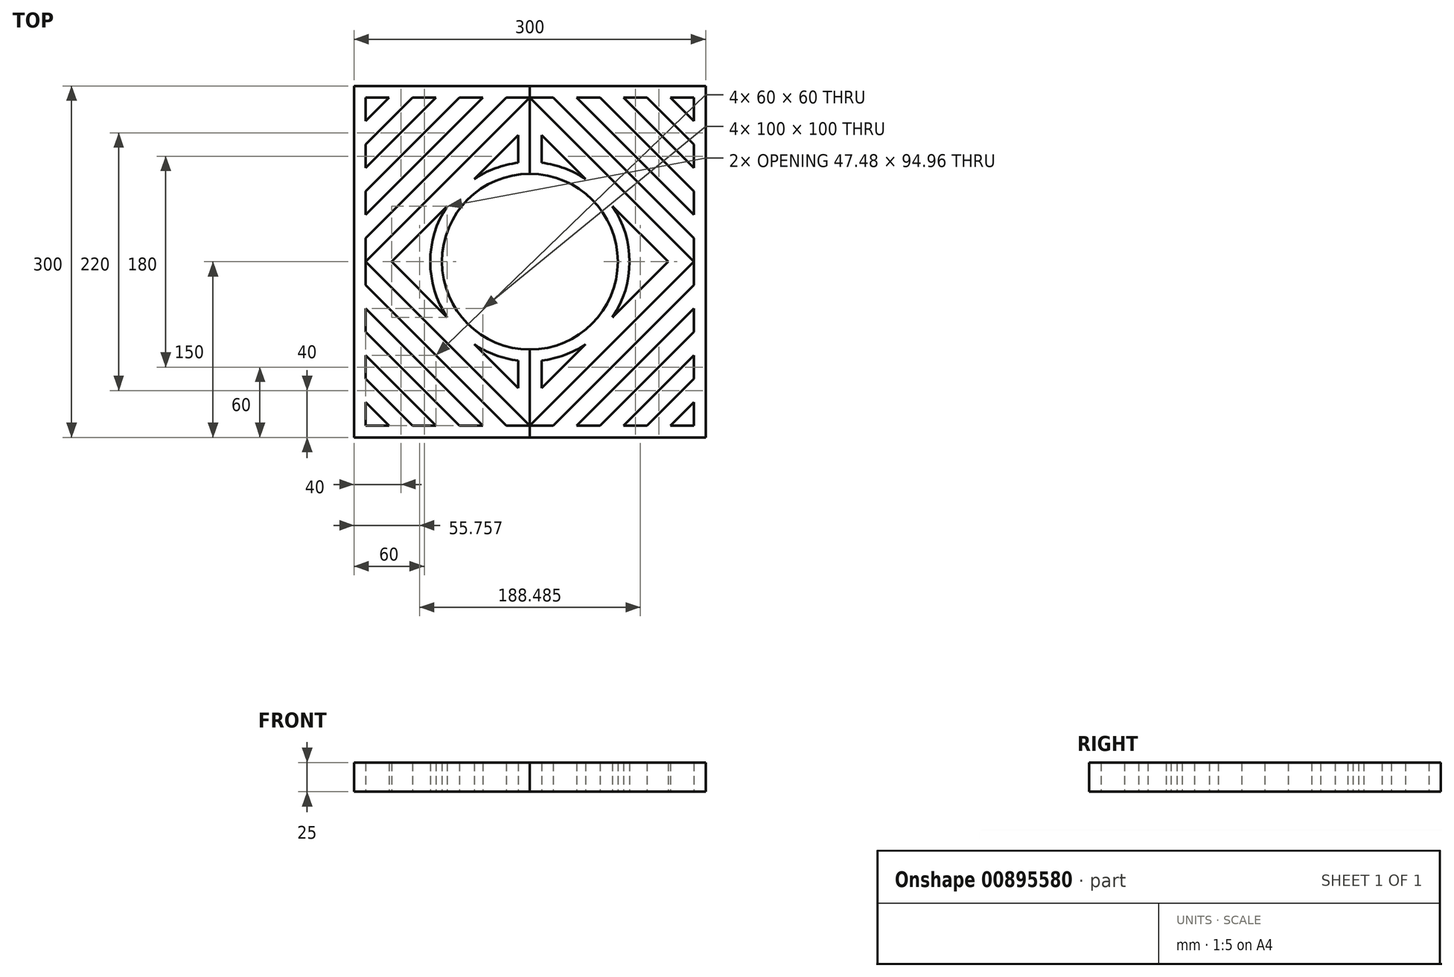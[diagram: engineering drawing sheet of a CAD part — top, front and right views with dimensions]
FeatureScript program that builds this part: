
annotation { "Feature Type Name" : "Feature", "Feature Type Description" : "" }
export const myFeature = defineFeature(function(context is Context, id is Id, definition is map)
    precondition{}
    {
        {
            var Q0;
            Q0=qCreatedBy(makeId("Top.planeOp"),FACE);
            var sketch = newSketch(context, id + "F0", { "sketchPlane" : qUnion([Q0])});
            skLineSegment(sketch, "E0.top", {"start": v(0, 150) * mm, "end": v(-150, 150) * mm});
            skLineSegment(sketch, "E0.right", {"start": v(-150, 0) * mm, "end": v(-150, 150) * mm});
            skPoint(sketch, "E0.middle", {"position": v(0, 0) * mm});
            skLineSegment(sketch, "E1.top", {"start": v(0, 140) * mm, "end": v(-80, 140) * mm});
            skLineSegment(sketch, "E1.right", {"start": v(-140, 0) * mm, "end": v(-140, 80) * mm});
            skLineSegment(sketch, "E2", {"start": v(0, 150) * mm, "end": v(0, 75) * mm, "construction": true});
            skLineSegment(sketch, "E3", {"start": v(-140, 100) * mm, "end": v(-100, 140) * mm});
            skLineSegment(sketch, "E4", {"start": v(-140, 80) * mm, "end": v(-80, 140) * mm});
            skLineSegment(sketch, "E5.trimOffspring", {"start": v(-100, 140) * mm, "end": v(-140, 140) * mm});
            skLineSegment(sketch, "E6.trimOffspring", {"start": v(-140, 100) * mm, "end": v(-140, 140) * mm});
            skLineSegment(sketch, "E7", {"start": v(0, 150) * mm, "end": v(0, 140) * mm});
            skArc(sketch, "E8", {"start": v(0, 75) * mm, "mid": v(-53.03, 53.03) * mm, "end": v(-75, 0) * mm});
            skLineSegment(sketch, "E9", {"start": v(0, 140) * mm, "end": v(0, 75) * mm});
            skArc(sketch, "E10.0", {"start": v(-10.04, 84.4) * mm, "mid": v(-63.55, 56.44) * mm, "end": v(-85, 0) * mm});
            skLineSegment(sketch, "E11", {"start": v(-150, 0) * mm, "end": v(-75, 0) * mm});
            skLineSegment(sketch, "E12", {"start": v(-140, 60) * mm, "end": v(-60, 140) * mm});
            skLineSegment(sketch, "E13", {"start": v(-40, 140) * mm, "end": v(-140, 40) * mm});
            skLineSegment(sketch, "E14", {"start": v(-20, 140) * mm, "end": v(-140, 20) * mm});
            skLineSegment(sketch, "E15", {"start": v(-10.04, 107.95) * mm, "end": v(-117.98, 0) * mm});
            skPoint(sketch, "E16.trimOffspring.end.orphan", {"position": v(-160, 0) * mm});
            skLineSegment(sketch, "E17", {"start": v(0, 140) * mm, "end": v(-140, 0) * mm});
            skLineSegment(sketch, "E18", {"start": v(-140, 120) * mm, "end": v(-120, 140) * mm});
            skLineSegment(sketch, "E19", {"start": v(-100, 140) * mm, "end": v(-80, 140) * mm});
            skLineSegment(sketch, "E20", {"start": v(-140, 100) * mm, "end": v(-140, 80) * mm});
            skPoint(sketch, "E0.bottom.end.orphan", {"position": v(-150, -150) * mm});
            skPoint(sketch, "E21.start.orphan", {"position": v(0, 107.5) * mm});
            skLineSegment(sketch, "E22", {"start": v(0, 85) * mm, "end": v(0, 117.98) * mm});
            skLineSegment(sketch, "E23", {"start": v(-10.04, 84.4) * mm, "end": v(-10.04, 107.95) * mm});
            skSolve(sketch);
        }
        {
            var Q0;
            {var subQ5=sQuery(id+"F0.wireOp",EDGE,"E0.bottom");Q0=makeQuery(id+"F0.imprint","IMPRINT",FACE,{"disambiguationData":[TD([[makeQuery(id+"F0.imprint","IMPRINT",EDGE,{"derivedFrom":subQ5}),-1.0]])]});}
            var Q1;
            {var subQ0=sQuery(id+"F0.wireOp",EDGE,"jHVn3feS-g2zb-SIal-xTdj-Eq9i8jqKTf0S");var subQ1=sQuery(id+"F0.wireOp",EDGE,"E8");var subQ2=makeQuery(id+"F0.imprint","INTERSECT",VERTEX,{"derivedFrom":[subQ1,subQ0]});Q1=makeQuery(id+"F0.imprint","IMPRINT",FACE,{"disambiguationData":[TD([[makeQuery(id+"F0.imprint","IMPRINT",EDGE,{"disambiguationData":[TD([[subQ2,1.0]])],"derivedFrom":subQ1}),-1.0]])]});}
            var Q2;
            {var subQ2=sQuery(id+"F0.wireOp",EDGE,"E15");Q2=makeQuery(id+"F0.imprint","IMPRINT",FACE,{"disambiguationData":[TD([[makeQuery(id+"F0.imprint","IMPRINT",EDGE,{"derivedFrom":subQ2}),-1.0]])]});}
            var Q3;
            {var subQ1=sQuery(id+"F0.wireOp",EDGE,"E9");var subQ5=sQuery(id+"F0.wireOp",EDGE,"E8");var subQ6=makeQuery(id+"F0.imprint","INTERSECT",VERTEX,{"derivedFrom":[subQ5,subQ1]});Q3=makeQuery(id+"F0.imprint","IMPRINT",FACE,{"disambiguationData":[TD([[makeQuery(id+"F0.imprint","IMPRINT",EDGE,{"disambiguationData":[TD([[subQ6,-1.0]])],"derivedFrom":subQ5}),-1.0]])]});}
            var Q4;
            {var subQ5=sQuery(id+"F0.wireOp",EDGE,"E1.bottom");Q4=makeQuery(id+"F0.imprint","IMPRINT",FACE,{"disambiguationData":[TD([[makeQuery(id+"F0.imprint","IMPRINT",EDGE,{"derivedFrom":subQ5}),-1.0]])]});}
            var Q5;
            {var subQ18=sQuery(id+"F0.wireOp",EDGE,"E0.top");Q5=makeQuery(id+"F0.imprint","IMPRINT",FACE,{"disambiguationData":[TD([[makeQuery(id+"F0.imprint","IMPRINT",EDGE,{"derivedFrom":subQ18}),1.0]])]});}
            var Q6;
            {var subQ0=sQuery(id+"F0.wireOp",EDGE,"E3");Q6=makeQuery(id+"F0.imprint","IMPRINT",FACE,{"disambiguationData":[TD([[makeQuery(id+"F0.imprint","IMPRINT",EDGE,{"derivedFrom":subQ0}),1.0]])]});}
            var Q7;
            {var subQ0=sQuery(id+"F0.wireOp",EDGE,"E4");Q7=makeQuery(id+"F0.imprint","IMPRINT",FACE,{"disambiguationData":[TD([[makeQuery(id+"F0.imprint","IMPRINT",EDGE,{"derivedFrom":subQ0}),-1.0]])]});}
            var Q8;
            {var subQ0=sQuery(id+"F0.wireOp",EDGE,"E13");Q8=makeQuery(id+"F0.imprint","IMPRINT",FACE,{"disambiguationData":[TD([[makeQuery(id+"F0.imprint","IMPRINT",EDGE,{"derivedFrom":subQ0}),1.0]])]});}
            extrude(context, id + "F1", {"entities" : qUnion([Q0, Q1, Q2, Q3, Q4, Q5, Q6, Q7, Q8]), "depth" : 25 * mm, "offsetDistance" : 25 * mm});
        }
        {
            var Q0;
            Q0=makeQuery(id+"F1.opExtrude","SWEPT_BODY",BODY,{"disambiguationData":[OSD([sQuery(id+"F0.wireOp",EDGE,"E0.top"),sQuery(id+"F0.wireOp",EDGE,"E0.right"),sQuery(id+"F0.wireOp",EDGE,"E1.top"),sQuery(id+"F0.wireOp",EDGE,"E1.right"),sQuery(id+"F0.wireOp",EDGE,"E3"),sQuery(id+"F0.wireOp",EDGE,"E4"),sQuery(id+"F0.wireOp",EDGE,"E5.trimOffspring"),sQuery(id+"F0.wireOp",EDGE,"E6.trimOffspring"),sQuery(id+"F0.wireOp",EDGE,"E7"),sQuery(id+"F0.wireOp",EDGE,"E11"),sQuery(id+"F0.wireOp",EDGE,"E12"),sQuery(id+"F0.wireOp",EDGE,"E13"),sQuery(id+"F0.wireOp",EDGE,"E14"),sQuery(id+"F0.wireOp",EDGE,"E18"),sQuery(id+"F0.wireOp",EDGE,"E19"),sQuery(id+"F0.wireOp",EDGE,"E20")])]});
            var Q1;
            Q1=makeQuery(id+"F1.opExtrude","SWEPT_BODY",BODY,{"disambiguationData":[OSD([sQuery(id+"F0.wireOp",EDGE,"E9"),sQuery(id+"F0.wireOp",EDGE,"E11"),sQuery(id+"F0.wireOp",EDGE,"E15"),sQuery(id+"F0.wireOp",EDGE,"E17")])]});
            var Q2;
            Q2=qCreatedBy(makeId("Front.planeOp"),FACE);
            mirror(context, id + "F2", {"entities" : qUnion([Q0, Q1]), "mirrorPlane" : qUnion([Q2])});
        }
        {
            var Q0;
            Q0=makeQuery(id+"F1.opExtrude","SWEPT_BODY",BODY,{"disambiguationData":[OSD([sQuery(id+"F0.wireOp",EDGE,"E8"),sQuery(id+"F0.wireOp",EDGE,"E9"),sQuery(id+"F0.wireOp",EDGE,"E10.0"),sQuery(id+"F0.wireOp",EDGE,"E11")])]});
            var Q1;
            Q1=qCreatedBy(makeId("Front.planeOp"),FACE);
            mirror(context, id + "F3", {"operationType" : NewBodyOperationType.ADD, "entities" : qUnion([Q0]), "mirrorPlane" : qUnion([Q1])});
        }
        {
            var Q0;
            Q0=makeQuery(id+"F1.opExtrude","SWEPT_BODY",BODY,{"disambiguationData":[OSD([sQuery(id+"F0.wireOp",EDGE,"E9"),sQuery(id+"F0.wireOp",EDGE,"E11"),sQuery(id+"F0.wireOp",EDGE,"E15"),sQuery(id+"F0.wireOp",EDGE,"E17")])]});
            var Q1;
            Q1=makeQuery(id+"F1.opExtrude","SWEPT_BODY",BODY,{"disambiguationData":[OSD([sQuery(id+"F0.wireOp",EDGE,"E0.top"),sQuery(id+"F0.wireOp",EDGE,"E0.right"),sQuery(id+"F0.wireOp",EDGE,"E1.top"),sQuery(id+"F0.wireOp",EDGE,"E1.right"),sQuery(id+"F0.wireOp",EDGE,"E3"),sQuery(id+"F0.wireOp",EDGE,"E4"),sQuery(id+"F0.wireOp",EDGE,"E5.trimOffspring"),sQuery(id+"F0.wireOp",EDGE,"E6.trimOffspring"),sQuery(id+"F0.wireOp",EDGE,"E7"),sQuery(id+"F0.wireOp",EDGE,"E11"),sQuery(id+"F0.wireOp",EDGE,"E12"),sQuery(id+"F0.wireOp",EDGE,"E13"),sQuery(id+"F0.wireOp",EDGE,"E14"),sQuery(id+"F0.wireOp",EDGE,"E18"),sQuery(id+"F0.wireOp",EDGE,"E19"),sQuery(id+"F0.wireOp",EDGE,"E20")])]});
            var Q2;
            Q2=makeQuery(id+"F2.opPattern","COPY",BODY,{"derivedFrom":makeQuery(id+"F1.opExtrude","SWEPT_BODY",BODY,{"disambiguationData":[OSD([sQuery(id+"F0.wireOp",EDGE,"E9"),sQuery(id+"F0.wireOp",EDGE,"E11"),sQuery(id+"F0.wireOp",EDGE,"E15"),sQuery(id+"F0.wireOp",EDGE,"E17")])]}),"instanceName":"1"});
            var Q3;
            Q3=makeQuery(id+"F2.opPattern","COPY",BODY,{"derivedFrom":makeQuery(id+"F1.opExtrude","SWEPT_BODY",BODY,{"disambiguationData":[OSD([sQuery(id+"F0.wireOp",EDGE,"E0.top"),sQuery(id+"F0.wireOp",EDGE,"E0.right"),sQuery(id+"F0.wireOp",EDGE,"E1.top"),sQuery(id+"F0.wireOp",EDGE,"E1.right"),sQuery(id+"F0.wireOp",EDGE,"E3"),sQuery(id+"F0.wireOp",EDGE,"E4"),sQuery(id+"F0.wireOp",EDGE,"E5.trimOffspring"),sQuery(id+"F0.wireOp",EDGE,"E6.trimOffspring"),sQuery(id+"F0.wireOp",EDGE,"E7"),sQuery(id+"F0.wireOp",EDGE,"E11"),sQuery(id+"F0.wireOp",EDGE,"E12"),sQuery(id+"F0.wireOp",EDGE,"E13"),sQuery(id+"F0.wireOp",EDGE,"E14"),sQuery(id+"F0.wireOp",EDGE,"E18"),sQuery(id+"F0.wireOp",EDGE,"E19"),sQuery(id+"F0.wireOp",EDGE,"E20")])]}),"instanceName":"1"});
            var Q4;
            Q4=makeQuery(id+"F1.opExtrude","SWEPT_BODY",BODY,{"disambiguationData":[OSD([sQuery(id+"F0.wireOp",EDGE,"E8"),sQuery(id+"F0.wireOp",EDGE,"E9"),sQuery(id+"F0.wireOp",EDGE,"E10.0"),sQuery(id+"F0.wireOp",EDGE,"E11")])]});
            var Q5;
            Q5=qCreatedBy(makeId("Right.planeOp"),FACE);
            mirror(context, id + "F4", {"entities" : qUnion([Q0, Q1, Q2, Q3, Q4]), "mirrorPlane" : qUnion([Q5])});
        }
    });
